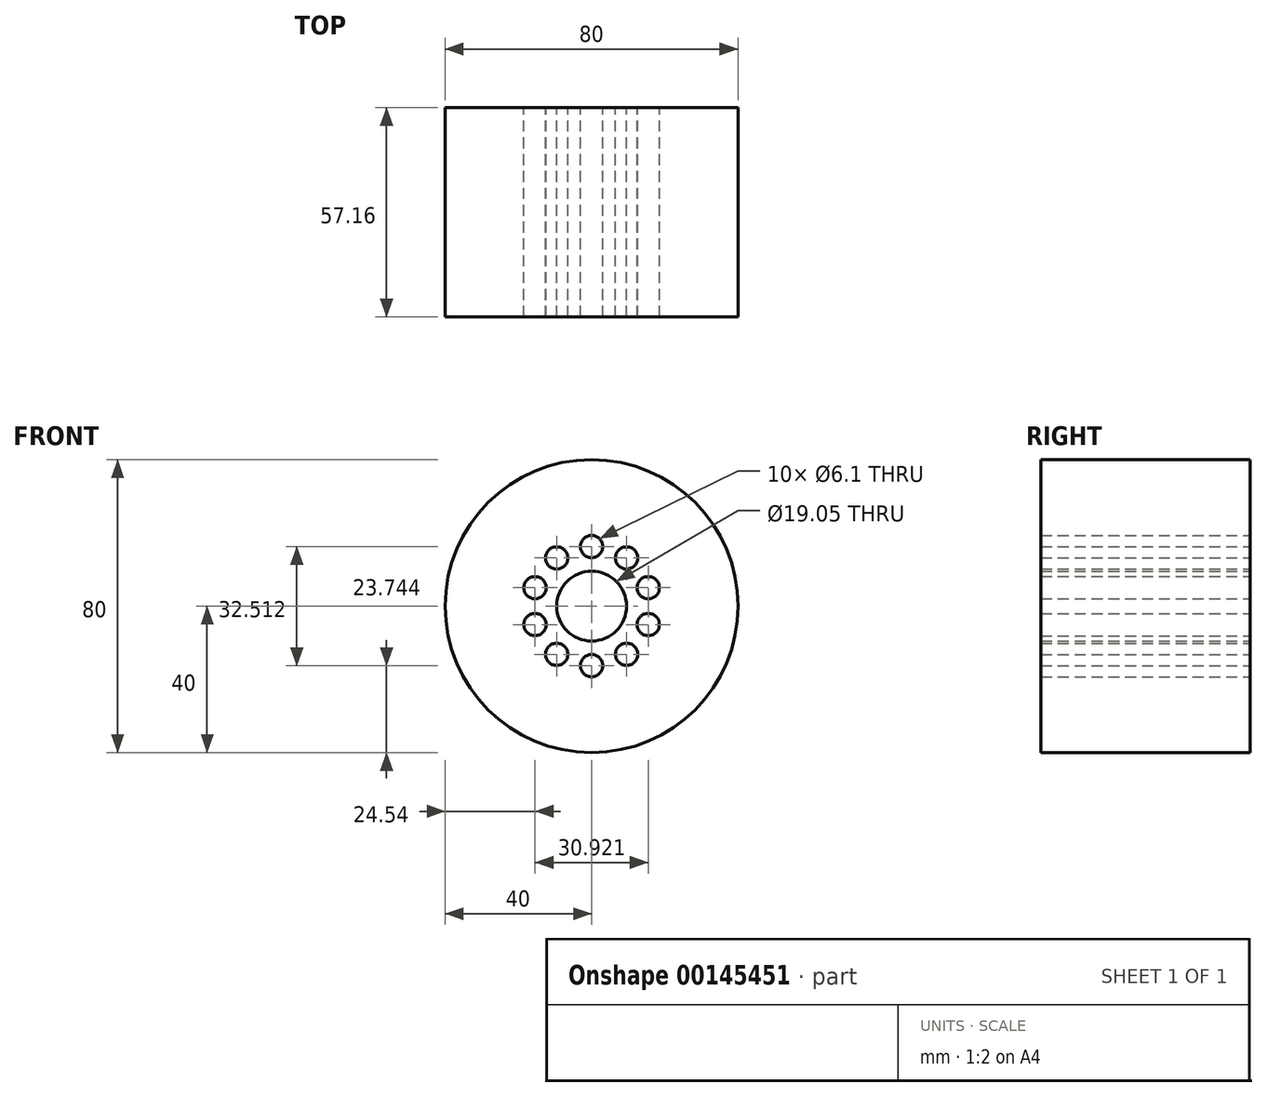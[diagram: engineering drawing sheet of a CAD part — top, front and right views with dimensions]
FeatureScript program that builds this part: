
annotation { "Feature Type Name" : "Feature", "Feature Type Description" : "" }
export const myFeature = defineFeature(function(context is Context, id is Id, definition is map)
    precondition{}
    {
        {
            var Q0;
            Q0=qCreatedBy(makeId("Front.planeOp"),FACE);
            var sketch = newSketch(context, id + "F0", { "sketchPlane" : qUnion([Q0])});
            skCircle(sketch, "E0", {"center": v(0, 0) * mm, "radius": 9.53 * mm});
            skCircle(sketch, "E1", {"center": v(0, 0) * mm, "radius": 16.26 * mm, "construction": true});
            skCircle(sketch, "E2", {"center": v(0, 0) * mm, "radius": 40 * mm});
            skCircle(sketch, "E3", {"center": v(0, 16.26) * mm, "radius": 3.05 * mm});
            skCircle(sketch, "E4.1.0", {"center": v(-9.56, 13.15) * mm, "radius": 3.05 * mm});
            skCircle(sketch, "E4.2.0", {"center": v(-15.46, 5.02) * mm, "radius": 3.05 * mm});
            skCircle(sketch, "E4.3.0", {"center": v(-15.46, -5.02) * mm, "radius": 3.05 * mm});
            skCircle(sketch, "E4.4.0", {"center": v(-9.56, -13.15) * mm, "radius": 3.05 * mm});
            skCircle(sketch, "E4.5.0", {"center": v(0, -16.26) * mm, "radius": 3.05 * mm});
            skCircle(sketch, "E4.6.0", {"center": v(9.56, -13.15) * mm, "radius": 3.05 * mm});
            skCircle(sketch, "E4.7.0", {"center": v(15.46, -5.02) * mm, "radius": 3.05 * mm});
            skCircle(sketch, "E4.8.0", {"center": v(15.46, 5.02) * mm, "radius": 3.05 * mm});
            skCircle(sketch, "E4.9.0", {"center": v(9.56, 13.15) * mm, "radius": 3.05 * mm});
            skSolve(sketch);
        }
        {
            var Q0;
            Q0 = qSketchRegion(id + "F0", true);
            extrude(context, id + "F1", {"entities" : qUnion([Q0]), "endBound" : BoundingType.SYMMETRIC, "depth" : 57.15 * mm});
        }
    });
